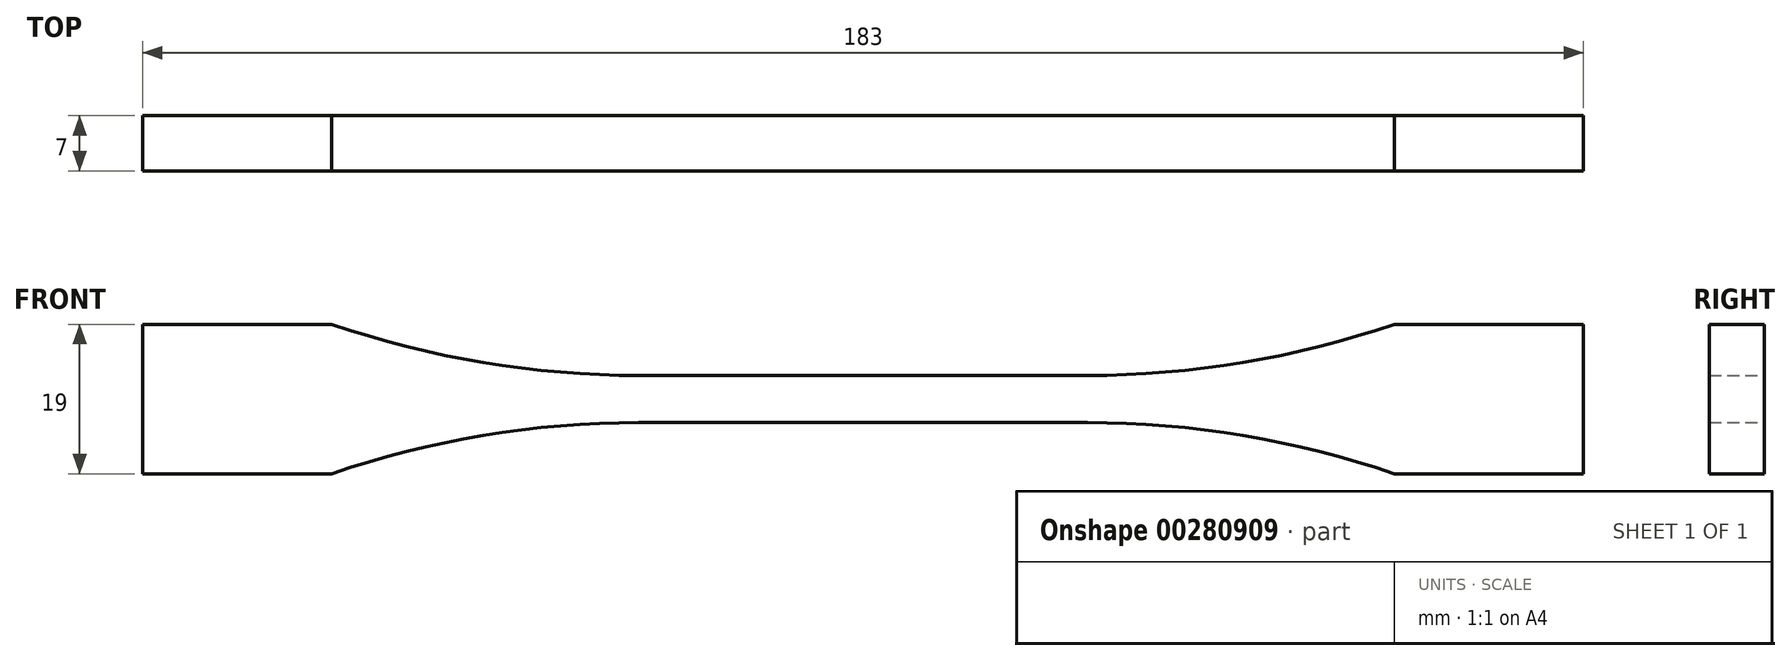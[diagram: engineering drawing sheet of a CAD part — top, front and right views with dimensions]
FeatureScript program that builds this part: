
annotation { "Feature Type Name" : "Feature", "Feature Type Description" : "" }
export const myFeature = defineFeature(function(context is Context, id is Id, definition is map)
    precondition{}
    {
        {
            var Q0;
            Q0=qCreatedBy(makeId("Front.planeOp"),FACE);
            var sketch = newSketch(context, id + "F0", { "sketchPlane" : qUnion([Q0])});
            skLineSegment(sketch, "E0", {"start": v(0, 3) * mm, "end": v(28.5, 3) * mm});
            skLineSegment(sketch, "E1", {"start": v(67.5, 9.5) * mm, "end": v(91.5, 9.5) * mm});
            skLineSegment(sketch, "E2", {"start": v(91.5, 9.5) * mm, "end": v(91.5, 0) * mm});
            skArc(sketch, "E3", {"start": v(28.5, 3) * mm, "mid": v(48.27, 4.64) * mm, "end": v(67.5, 9.5) * mm});
            skLineSegment(sketch, "E4.MirrorCS", {"start": v(67.5, -9.5) * mm, "end": v(91.5, -9.5) * mm});
            skArc(sketch, "E5.MirrorCS", {"start": v(28.5, -3) * mm, "mid": v(48.27, -4.64) * mm, "end": v(67.5, -9.5) * mm});
            skLineSegment(sketch, "E6.MirrorCS", {"start": v(91.5, -9.5) * mm, "end": v(91.5, 0) * mm});
            skLineSegment(sketch, "E7.MirrorCS", {"start": v(0, -3) * mm, "end": v(28.5, -3) * mm});
            skLineSegment(sketch, "E8.MirrorCS", {"start": v(0, -3) * mm, "end": v(-28.5, -3) * mm});
            skLineSegment(sketch, "E9.MirrorCS", {"start": v(-91.5, -9.5) * mm, "end": v(-91.5, 0) * mm});
            skLineSegment(sketch, "E10.MirrorCS", {"start": v(0, 3) * mm, "end": v(-28.5, 3) * mm});
            skLineSegment(sketch, "E11.MirrorCS", {"start": v(-67.5, 9.5) * mm, "end": v(-91.5, 9.5) * mm});
            skLineSegment(sketch, "E12.MirrorCS", {"start": v(-91.5, 9.5) * mm, "end": v(-91.5, 0) * mm});
            skArc(sketch, "E13.MirrorCS", {"start": v(-28.5, -3) * mm, "mid": v(-48.27, -4.64) * mm, "end": v(-67.5, -9.5) * mm});
            skLineSegment(sketch, "E14.MirrorCS", {"start": v(-67.5, -9.5) * mm, "end": v(-91.5, -9.5) * mm});
            skArc(sketch, "E15.MirrorCS", {"start": v(-28.5, 3) * mm, "mid": v(-48.27, 4.64) * mm, "end": v(-67.5, 9.5) * mm});
            skSolve(sketch);
        }
        {
            var Q0;
            Q0=makeQuery(id+"F0.imprint","IMPRINT",FACE,{"disambiguationData":[TD([[makeQuery(id+"F0.imprint","IMPRINT",EDGE,{"derivedFrom":sQuery(id+"F0.wireOp",EDGE,"E0")}),-1.0]])]});
            extrude(context, id + "F1", {"entities" : qUnion([Q0]), "depth" : 7 * mm});
        }
    });
